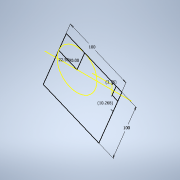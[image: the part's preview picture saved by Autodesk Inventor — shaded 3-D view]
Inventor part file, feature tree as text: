
AUTODESK INVENTOR PART (.ipt)
format: ipt  version: 2022 (Build 260153070, 153G)  size: 100,352 bytes
history: native  units: mm
features: other x5, reference x3, sketch x1
ambient origin geometry x8: Origin, YZ Plane, XZ Plane, XY Plane, X Axis, Y Axis, Z Axis, Center Point
feature tree (9):
  sketch  "Sketch1"  dims[d0=90.0deg d4=100.0mm d5=22.5deg d6=10.267698mm d7=3.760459mm d8=100.0mm]
  reference  "Reference1"
  reference  "Reference2"
  reference  "Reference3"
  other  "<userpath> laptop\Desktop\SumoBot\FullBot.iam"
  other  "FullBot.iam"
  other  "TT wheel:1"
  other  "MotorEncoderAssembly:1"
  other  "TTmotor:1"
